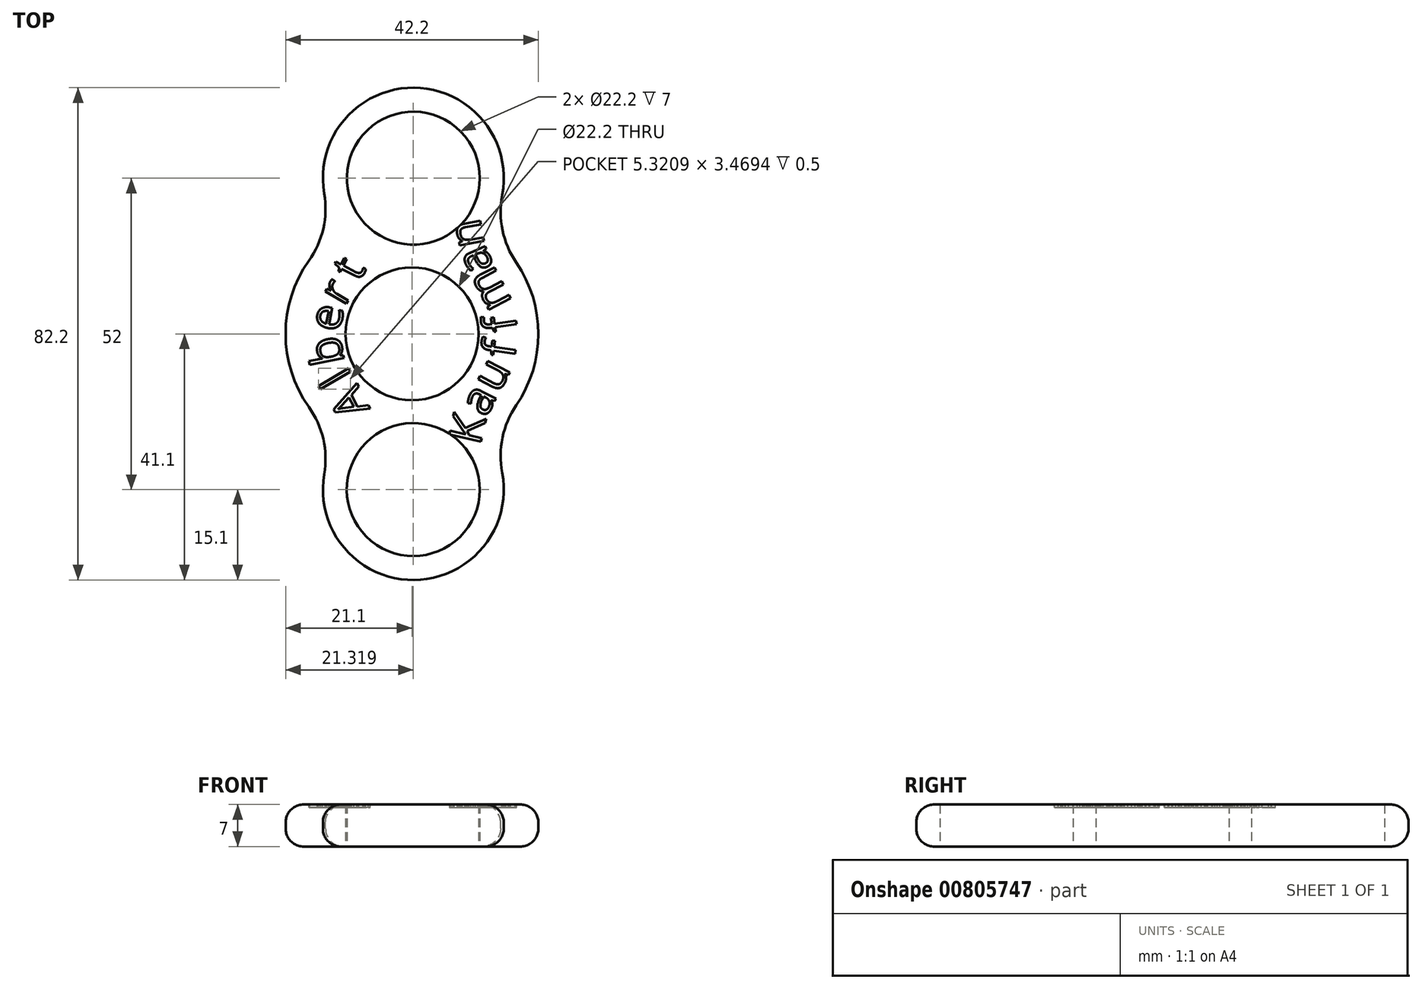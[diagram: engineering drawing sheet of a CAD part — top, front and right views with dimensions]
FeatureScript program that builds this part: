
annotation { "Feature Type Name" : "Feature", "Feature Type Description" : "" }
export const myFeature = defineFeature(function(context is Context, id is Id, definition is map)
    precondition{}
    {
        {
            var Q0;
            Q0=qCreatedBy(makeId("Top.planeOp"),FACE);
            var sketch = newSketch(context, id + "F0", { "sketchPlane" : qUnion([Q0])});
            skCircle(sketch, "E0", {"center": v(0, 0) * mm, "radius": 11.1 * mm});
            skCircle(sketch, "E1", {"center": v(0.22, 26) * mm, "radius": 11.1 * mm});
            skCircle(sketch, "E2", {"center": v(0.22, -26) * mm, "radius": 11.1 * mm});
            skCircle(sketch, "E3.0", {"center": v(0.22, 26) * mm, "radius": 15.1 * mm, "construction": true});
            skCircle(sketch, "E4.0", {"center": v(0.22, -26) * mm, "radius": 15.1 * mm, "construction": true});
            skCircle(sketch, "E5.0", {"center": v(0, 0) * mm, "radius": 21.1 * mm, "construction": true});
            skArc(sketch, "E6", {"start": v(-12.1, 17.28) * mm, "mid": v(0.35, 41.1) * mm, "end": v(12.4, 17.07) * mm});
            skArc(sketch, "E7", {"start": v(12.4, 17.07) * mm, "mid": v(21.1, 0) * mm, "end": v(12.4, -17.07) * mm});
            skArc(sketch, "E8", {"start": v(12.4, -17.07) * mm, "mid": v(0.35, -41.1) * mm, "end": v(-12.1, -17.28) * mm});
            skArc(sketch, "E9", {"start": v(-12.1, -17.28) * mm, "mid": v(-21.1, 0) * mm, "end": v(-12.1, 17.28) * mm});
            skSolve(sketch);
        }
        {
            var Q0;
            Q0=makeQuery(id+"F0.imprint","IMPRINT",FACE,{"disambiguationData":[TD([[makeQuery(id+"F0.imprint","IMPRINT",EDGE,{"derivedFrom":sQuery(id+"F0.wireOp",EDGE,"E0")}),-1.0]])]});
            extrude(context, id + "F1", {"entities" : qUnion([Q0]), "depth" : 7 * mm, "offsetDistance" : 25 * mm});
        }
        {
            var Q0;
            Q0=makeQuery(id+"F1.opExtrude","SWEPT_EDGE",EDGE,{"disambiguationData":[OSD([sQuery(id+"F0.wireOp",EDGE,"E6"),sQuery(id+"F0.wireOp",EDGE,"E9")])]});
            var Q1;
            Q1=makeQuery(id+"F1.opExtrude","SWEPT_EDGE",EDGE,{"disambiguationData":[OSD([sQuery(id+"F0.wireOp",EDGE,"E8"),sQuery(id+"F0.wireOp",EDGE,"E9")])]});
            var Q2;
            Q2=makeQuery(id+"F1.opExtrude","SWEPT_EDGE",EDGE,{"disambiguationData":[OSD([sQuery(id+"F0.wireOp",EDGE,"E7"),sQuery(id+"F0.wireOp",EDGE,"E8")])]});
            var Q3;
            Q3=makeQuery(id+"F1.opExtrude","SWEPT_EDGE",EDGE,{"disambiguationData":[OSD([sQuery(id+"F0.wireOp",EDGE,"E6"),sQuery(id+"F0.wireOp",EDGE,"E7")])]});
            fillet(context, id + "F2", {"entities" : qUnion([Q0, Q1, Q2, Q3]), "radius" : 15 * mm, "tangentPropagation" : true, "allowEdgeOverflow" : false});
        }
        {
            var Q0;
            Q0=makeQuery(id+"F1.opExtrude","CAP_EDGE",EDGE,{"disambiguationData":[OSD([sQuery(id+"F0.wireOp",EDGE,"E9")])],"isStart":false});
            var Q1;
            Q1=makeQuery(id+"F1.opExtrude","CAP_EDGE",EDGE,{"disambiguationData":[OSD([sQuery(id+"F0.wireOp",EDGE,"E7")])],"isStart":true});
            fillet(context, id + "F3", {"entities" : qUnion([Q0, Q1]), "radius" : 3 * mm, "tangentPropagation" : true, "allowEdgeOverflow" : false});
        }
        {
            var Q0;
            Q0=makeQuery(id+"F1.opExtrude","CAP_FACE",FACE,{"disambiguationData":[OSD([sQuery(id+"F0.wireOp",EDGE,"E0"),sQuery(id+"F0.wireOp",EDGE,"E1"),sQuery(id+"F0.wireOp",EDGE,"E2"),sQuery(id+"F0.wireOp",EDGE,"E6"),sQuery(id+"F0.wireOp",EDGE,"E7"),sQuery(id+"F0.wireOp",EDGE,"E8"),sQuery(id+"F0.wireOp",EDGE,"E9")])],"isStart":false});
            var sketch = newSketch(context, id + "F4", { "sketchPlane" : qUnion([Q0])});
            skText(sketch, "E10", { "text": "A\n", "fontName": "OpenSans-Regular.ttf"});
            skText(sketch, "E11", { "text": "l", "fontName": "OpenSans-Regular.ttf"});
            skText(sketch, "E12", { "text": "b", "fontName": "OpenSans-Regular.ttf"});
            skText(sketch, "E13", { "text": "e", "fontName": "OpenSans-Regular.ttf"});
            skCircle(sketch, "E14", {"center": v(0, 0) * mm, "radius": 11.5 * mm, "construction": true});
            skText(sketch, "E15", { "text": "r", "fontName": "OpenSans-Regular.ttf"});
            skText(sketch, "E16", { "text": "t", "fontName": "OpenSans-Regular.ttf"});
            skText(sketch, "E17", { "text": "K", "fontName": "OpenSans-Regular.ttf"});
            skText(sketch, "E18", { "text": "a", "fontName": "OpenSans-Regular.ttf"});
            skText(sketch, "E19", { "text": "u", "fontName": "OpenSans-Regular.ttf"});
            skText(sketch, "E20", { "text": "f", "fontName": "OpenSans-Regular.ttf"});
            skText(sketch, "E21", { "text": "f", "fontName": "OpenSans-Regular.ttf"});
            skText(sketch, "E22", { "text": "m", "fontName": "OpenSans-Regular.ttf"});
            skText(sketch, "E23", { "text": "a", "fontName": "OpenSans-Regular.ttf"});
            skText(sketch, "E24", { "text": "n", "fontName": "OpenSans-Regular.ttf"});
            const initialGuessF4  = {"E10": [-0.00697, -0.0125, -0.4567, 0.88962, 0.0055], "E11": [-0.00997, -0.00687, -0.50564, 0.86274, 0.0055], "E12": [-0.01125, -0.00466, -0.19517, 0.98077, 0.0055], "E13": [-0.01216, 0.00016, 0.19296, 0.9812, 0.0055], "E15": [-0.01128, 0.00448, 0.49958, 0.86627, 0.0055], "E16": [-0.00885, 0.00856, 0.4637, 0.886, 0.0055], "E17": [0.01133, -0.01875, 0.22722, 0.97384, 0.0055], "E18": [0.01238, -0.01403, 0.4523, 0.89186, 0.0055], "E19": [0.01446, -0.01003, 0.45874, 0.88857, 0.00553], "E20": [0.0171, -0.00415, 0.14057, 0.99007, 0.0055], "E21": [0.01758, 0.00077, -0.14057, 0.99007, 0.0055], "E22": [0.01677, 0.00536, -0.46427, 0.8857, 0.0055], "E23": [0.01366, 0.0113, -0.39613, 0.9182, 0.0055], "E24": [0.0121, 0.01487, -0.17699, 0.98421, 0.0055]};
            skSetInitialGuess(sketch, initialGuessF4);
            skSolve(sketch);
        }
        {
            var Q0;
            Q0 = qSketchRegion(id + "F4", true);
            extrude(context, id + "F5", {"entities" : qUnion([Q0]), "operationType" : NewBodyOperationType.REMOVE, "oppositeDirection" : true, "depth" : .5 * mm, "offsetDistance" : 25 * mm});
        }
    });
